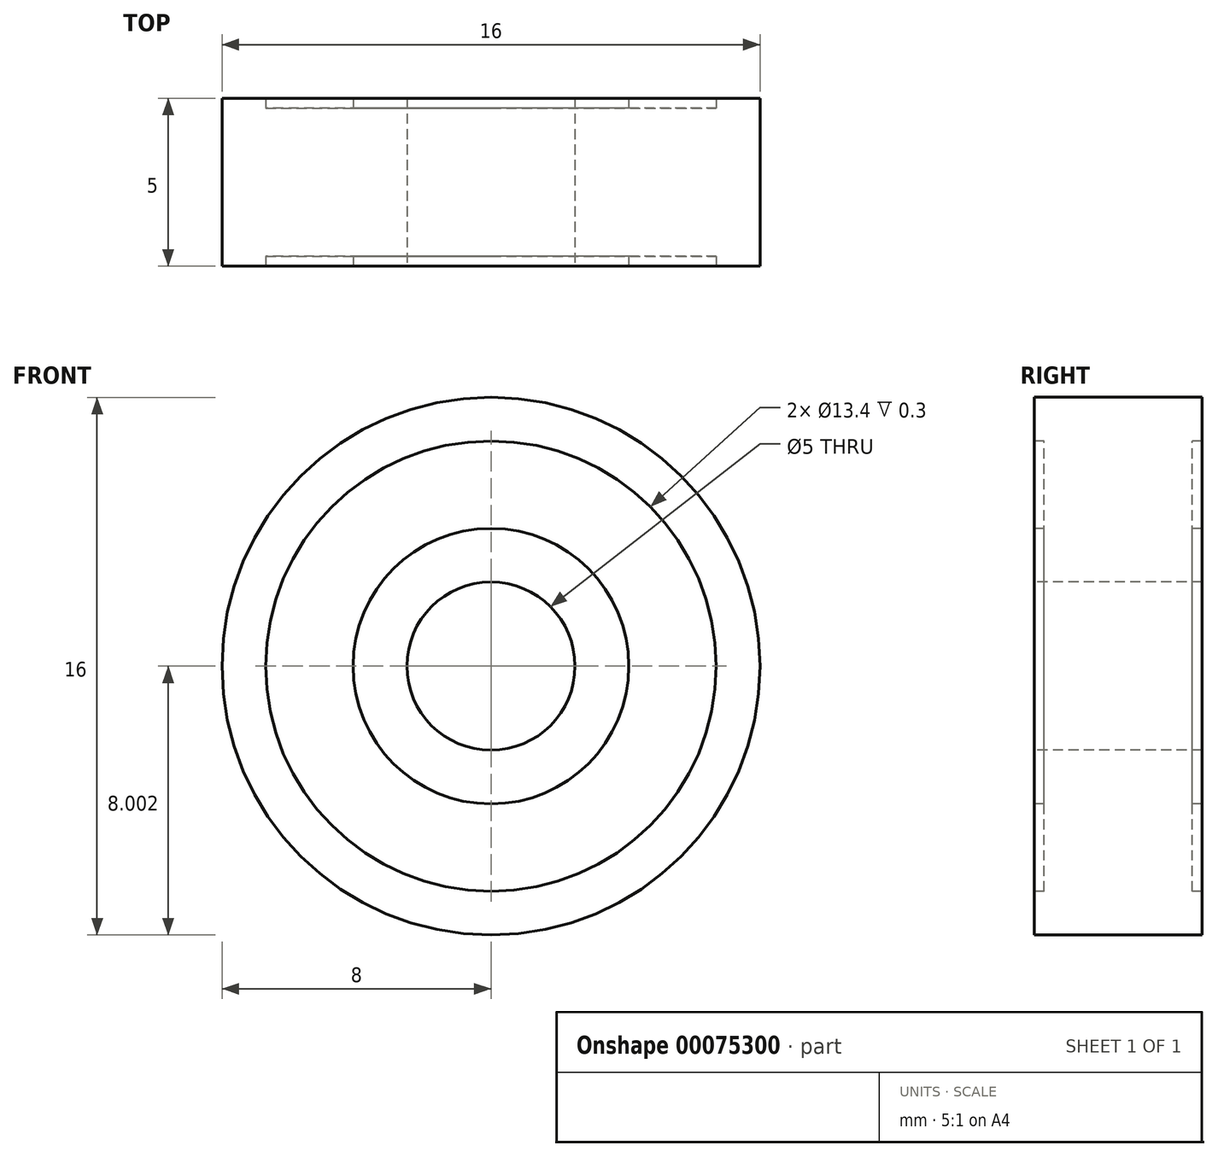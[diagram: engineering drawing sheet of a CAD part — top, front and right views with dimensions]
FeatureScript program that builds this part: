
annotation { "Feature Type Name" : "Feature", "Feature Type Description" : "" }
export const myFeature = defineFeature(function(context is Context, id is Id, definition is map)
    precondition{}
    {
        {
            var Q0;
            Q0=qCreatedBy(makeId("Right.planeOp"),FACE);
            var sketch = newSketch(context, id + "F0", { "sketchPlane" : qUnion([Q0])});
            skLineSegment(sketch, "E0", {"start": v(-2.6, 3.06) * mm, "end": v(-2.6, 1.76) * mm});
            skLineSegment(sketch, "E1", {"start": v(-2.6, 1.76) * mm, "end": v(-2.3, 1.76) * mm});
            skLineSegment(sketch, "E2", {"start": v(-2.3, 1.76) * mm, "end": v(-2.3, -0.84) * mm});
            skLineSegment(sketch, "E3", {"start": v(-2.3, -0.84) * mm, "end": v(-2.6, -0.84) * mm});
            skLineSegment(sketch, "E4", {"start": v(-2.6, -0.84) * mm, "end": v(-2.6, -2.44) * mm});
            skLineSegment(sketch, "E5", {"start": v(-2.6, -2.44) * mm, "end": v(2.4, -2.44) * mm});
            skLineSegment(sketch, "E6", {"start": v(2.4, -2.44) * mm, "end": v(2.4, -0.84) * mm});
            skLineSegment(sketch, "E7", {"start": v(2.4, -0.84) * mm, "end": v(2.1, -0.84) * mm});
            skLineSegment(sketch, "E8", {"start": v(2.1, -0.84) * mm, "end": v(2.1, 1.76) * mm});
            skLineSegment(sketch, "E9", {"start": v(2.1, 1.76) * mm, "end": v(2.4, 1.76) * mm});
            skLineSegment(sketch, "E10", {"start": v(2.4, 1.76) * mm, "end": v(2.4, 3.06) * mm});
            skLineSegment(sketch, "E11", {"start": v(2.4, 3.06) * mm, "end": v(-2.6, 3.06) * mm});
            skLineSegment(sketch, "E12", {"start": v(-2.6, -4.94) * mm, "end": v(4.93, -4.94) * mm, "construction": true});
            skSolve(sketch);
        }
        {
            var Q0;
            Q0=makeQuery(id+"F0.imprint","IMPRINT",FACE,{"disambiguationData":[TD([[makeQuery(id+"F0.imprint","IMPRINT",EDGE,{"derivedFrom":sQuery(id+"F0.wireOp",EDGE,"E0")}),1.0]])]});
            var Q1;
            Q1=sQuery(id+"F0.wireOp",EDGE,"E12");
            revolve(context, id + "F1", {"entities" : qUnion([Q0]), "axis" : qUnion([Q1]), "revolveType" : RevolveType.FULL});
        }
    });
